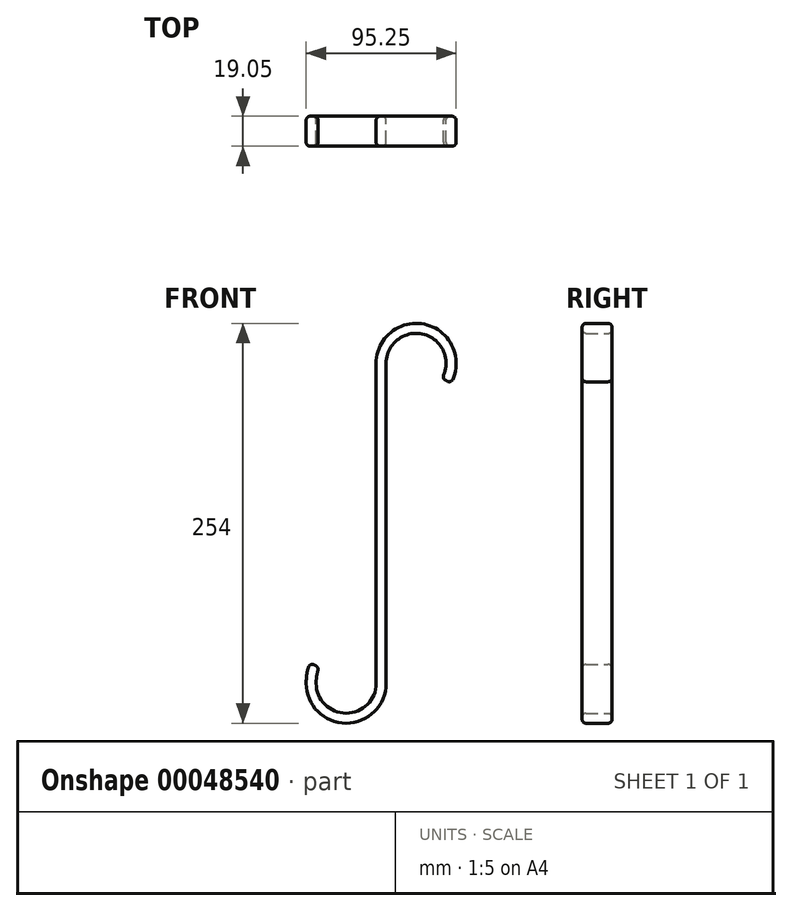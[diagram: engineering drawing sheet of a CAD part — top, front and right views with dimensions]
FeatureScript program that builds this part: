
annotation { "Feature Type Name" : "Feature", "Feature Type Description" : "" }
export const myFeature = defineFeature(function(context is Context, id is Id, definition is map)
    precondition{}
    {
        {
            var Q0;
            Q0=qCreatedBy(makeId("Front.planeOp"),FACE);
            var sketch = newSketch(context, id + "F0", { "sketchPlane" : qUnion([Q0])});
            skLineSegment(sketch, "E0", {"start": v(-25.4, 0) * mm, "end": v(-25.4, -203.2) * mm});
            skArc(sketch, "E1", {"start": v(-25.4, 0) * mm, "mid": v(0, 25.4) * mm, "end": v(25.4, 0) * mm});
            skLineSegment(sketch, "E2", {"start": v(-19.05, 0) * mm, "end": v(-19.05, -203.2) * mm});
            skArc(sketch, "E3", {"start": v(-19.05, -203.2) * mm, "mid": v(-44.45, -228.6) * mm, "end": v(-69.85, -203.2) * mm});
            skArc(sketch, "E4", {"start": v(-25.4, -203.2) * mm, "mid": v(-44.45, -222.25) * mm, "end": v(-63.5, -203.2) * mm});
            skLineSegment(sketch, "E5", {"start": v(0, 0) * mm, "end": v(0, -203.2) * mm, "construction": true});
            skLineSegment(sketch, "E6", {"start": v(-44.45, -203.2) * mm, "end": v(-88.48, -177.78) * mm, "construction": true});
            skLineSegment(sketch, "E7", {"start": v(0, 0) * mm, "end": v(34.56, -19.95) * mm, "construction": true});
            skArc(sketch, "E8", {"start": v(-63.5, -203.2) * mm, "mid": v(-63.07, -198.12) * mm, "end": v(-61.8, -193.18) * mm});
            skArc(sketch, "E9", {"start": v(-69.85, -203.2) * mm, "mid": v(-69.2, -196.48) * mm, "end": v(-67.3, -190) * mm});
            skLineSegment(sketch, "E10", {"start": v(-67.3, -190) * mm, "end": v(-61.8, -193.18) * mm});
            skArc(sketch, "E11", {"start": v(-19.05, 0) * mm, "mid": v(4.93, 18.4) * mm, "end": v(16.5, -9.52) * mm});
            skArc(sketch, "E12", {"start": v(25.4, 0) * mm, "mid": v(24.53, -6.57) * mm, "end": v(22, -12.7) * mm});
            skLineSegment(sketch, "E13", {"start": v(16.5, -9.53) * mm, "end": v(22, -12.7) * mm});
            skSolve(sketch);
        }
        {
            var Q0;
            Q0=makeQuery(id+"F0.imprint","IMPRINT",FACE,{"disambiguationData":[TD([[makeQuery(id+"F0.imprint","IMPRINT",EDGE,{"derivedFrom":sQuery(id+"F0.wireOp",EDGE,"E0")}),1.0]])]});
            var Q1;
            Q1=makeQuery(id+"F0.imprint","IMPRINT",FACE,{"disambiguationData":[TD([[makeQuery(id+"F0.imprint","IMPRINT",EDGE,{"derivedFrom":sQuery(id+"F0.wireOp",EDGE,"qGwicptO-gK2j-Kfag-Chg2-fPSLUECn81Ir")}),1.0]])]});
            var Q2;
            Q2=makeQuery(id+"F0.imprint","IMPRINT",FACE,{"disambiguationData":[TD([[makeQuery(id+"F0.imprint","IMPRINT",EDGE,{"derivedFrom":sQuery(id+"F0.wireOp",EDGE,"xNmMEBZU-oUyY-ZiBH-kAaP-bqtLUd6SUk8f")}),1.0]])]});
            extrude(context, id + "F1", {"entities" : qUnion([Q0, Q1, Q2]), "depth" : 19.05 * mm, "offsetDistance" : 25.4 * mm});
        }
        {
            var Q0;
            Q0=makeQuery(id+"F1.opExtrude","SWEPT_FACE",FACE,{"disambiguationData":[OSD([sQuery(id+"F0.wireOp",EDGE,"E10")])]});
            var Q1;
            Q1=makeQuery(id+"F1.opExtrude","SWEPT_FACE",FACE,{"disambiguationData":[OSD([sQuery(id+"F0.wireOp",EDGE,"E13")])]});
            var Q2;
            Q2=makeQuery(id+"F1.opExtrude","CAP_FACE",FACE,{"disambiguationData":[OSD([sQuery(id+"F0.wireOp",EDGE,"E0"),sQuery(id+"F0.wireOp",EDGE,"E1"),sQuery(id+"F0.wireOp",EDGE,"E2"),sQuery(id+"F0.wireOp",EDGE,"e197ccb5-3c14-4947-97bf-6bcbffad2c73"),sQuery(id+"F0.wireOp",EDGE,"E3"),sQuery(id+"F0.wireOp",EDGE,"E4"),sQuery(id+"F0.wireOp",EDGE,"E8"),sQuery(id+"F0.wireOp",EDGE,"E9"),sQuery(id+"F0.wireOp",EDGE,"E10"),sQuery(id+"F0.wireOp",EDGE,"E11"),sQuery(id+"F0.wireOp",EDGE,"E12"),sQuery(id+"F0.wireOp",EDGE,"E13")])],"isStart":true});
            var Q3;
            Q3=makeQuery(id+"F1.opExtrude","CAP_FACE",FACE,{"disambiguationData":[OSD([sQuery(id+"F0.wireOp",EDGE,"E0"),sQuery(id+"F0.wireOp",EDGE,"E1"),sQuery(id+"F0.wireOp",EDGE,"E2"),sQuery(id+"F0.wireOp",EDGE,"e197ccb5-3c14-4947-97bf-6bcbffad2c73"),sQuery(id+"F0.wireOp",EDGE,"E3"),sQuery(id+"F0.wireOp",EDGE,"E4"),sQuery(id+"F0.wireOp",EDGE,"E8"),sQuery(id+"F0.wireOp",EDGE,"E9"),sQuery(id+"F0.wireOp",EDGE,"E10"),sQuery(id+"F0.wireOp",EDGE,"E11"),sQuery(id+"F0.wireOp",EDGE,"E12"),sQuery(id+"F0.wireOp",EDGE,"E13")])],"isStart":false});
            fillet(context, id + "F2", {"entities" : qUnion([Q0, Q1, Q2, Q3]), "radius" : 2.54 * mm, "tangentPropagation" : true, "allowEdgeOverflow" : false});
        }
    });
